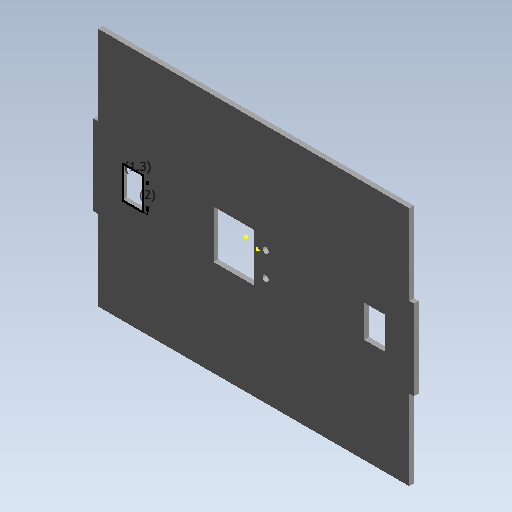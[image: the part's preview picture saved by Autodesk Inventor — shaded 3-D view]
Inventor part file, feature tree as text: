
AUTODESK INVENTOR PART (.ipt)
format: ipt  version: 2020 (Build 240168000, 168)  size: 192,512 bytes
history: native  units: mm (DEFAULTED — no unit token found)
features: sketch x20, extrude x13
ambient origin geometry x8: Origin, YZ Plane, XZ Plane, XY Plane, X Axis, Y Axis, Z Axis, Center Point
bodies: Solid1 (feature_tree)
feature tree (33):
  extrude  "Extrusion1"  Depth=3.0mm TaperAngle=0.0deg
  sketch  "Sketch2"  dims[d17=3.0mm d18=50.0mm]
  sketch  "Sketch3"  dims[d19=3.0mm d20=0.0mm d21=50.0mm]
  extrude  "Extrusion2"  Depth=50.0mm
  extrude  "Extrusion3"  Depth=50.0mm
  extrude  "Extrusion4"  Depth=3.0mm TaperAngle=0.0deg
  extrude  "Extrusion5"  Depth=3.0mm
  extrude  "Extrusion6"  Depth=15.0mm
  sketch  "Sketch9"  dims[d75=30.0mm d76=0.0mm d77=3.0mm d78=0.0mm]
  extrude  "Extrusion7"  Depth=3.0mm TaperAngle=0.0deg
  extrude  "Extrusion8"  Depth=30.0mm TaperAngle=0.0deg
  sketch  "Sketch12"  dims[d103=20.0mm d64=5.0mm]
  sketch  "Sketch13"  dims[d65=0.872665mm]
  extrude  "Extrusion9"  Depth=3.0mm TaperAngle=0.0deg
  extrude  "Extrusion10"  Depth=3.0mm TaperAngle=0.0deg
  extrude  "Extrusion11"  Depth=13.0mm
  extrude  "Extrusion12"  Depth=5.0mm
  extrude  "Extrusion13"  [1 undecoded]
  sketch  "Sketch19"
  sketch  "Sketch20"
  sketch  "Sketch1"  dims[d2=3.0mm d3=0.0mm d15=3.0mm d16=0.0mm]
  sketch  "Sketch4"  dims[d22=3.0mm d23=3.0mm d24=0.0mm]
  sketch  "Sketch5"  dims[d25=50.0mm d26=3.0mm]
  sketch  "Sketch6"  dims[d27=3.0mm d28=0.0mm d32=15.0mm]
  sketch  "Sketch7"  dims[d33=30.0mm d34=3.0mm d35=0.0mm]
  sketch  "Sketch8"  dims[d36=30.0mm d37=0.0mm d62=21.5mm d63=0.0mm]
  sketch  "Sketch10"  dims[d86=3.0mm d87=0.0mm d90=3.0mm d91=0.0mm]
  sketch  "Sketch11"  dims[d100=3.0mm d101=0.0mm d102=13.0mm]
  sketch  "Sketch14"
  sketch  "Sketch15"
  sketch  "Sketch16"
  sketch  "Sketch17"
  sketch  "Sketch18"
note: 1 required parameter value undecoded (feature->parameter linkage not recoverable at this tier; creation-order binding heuristic only, values carry confidence <= 0.55)
